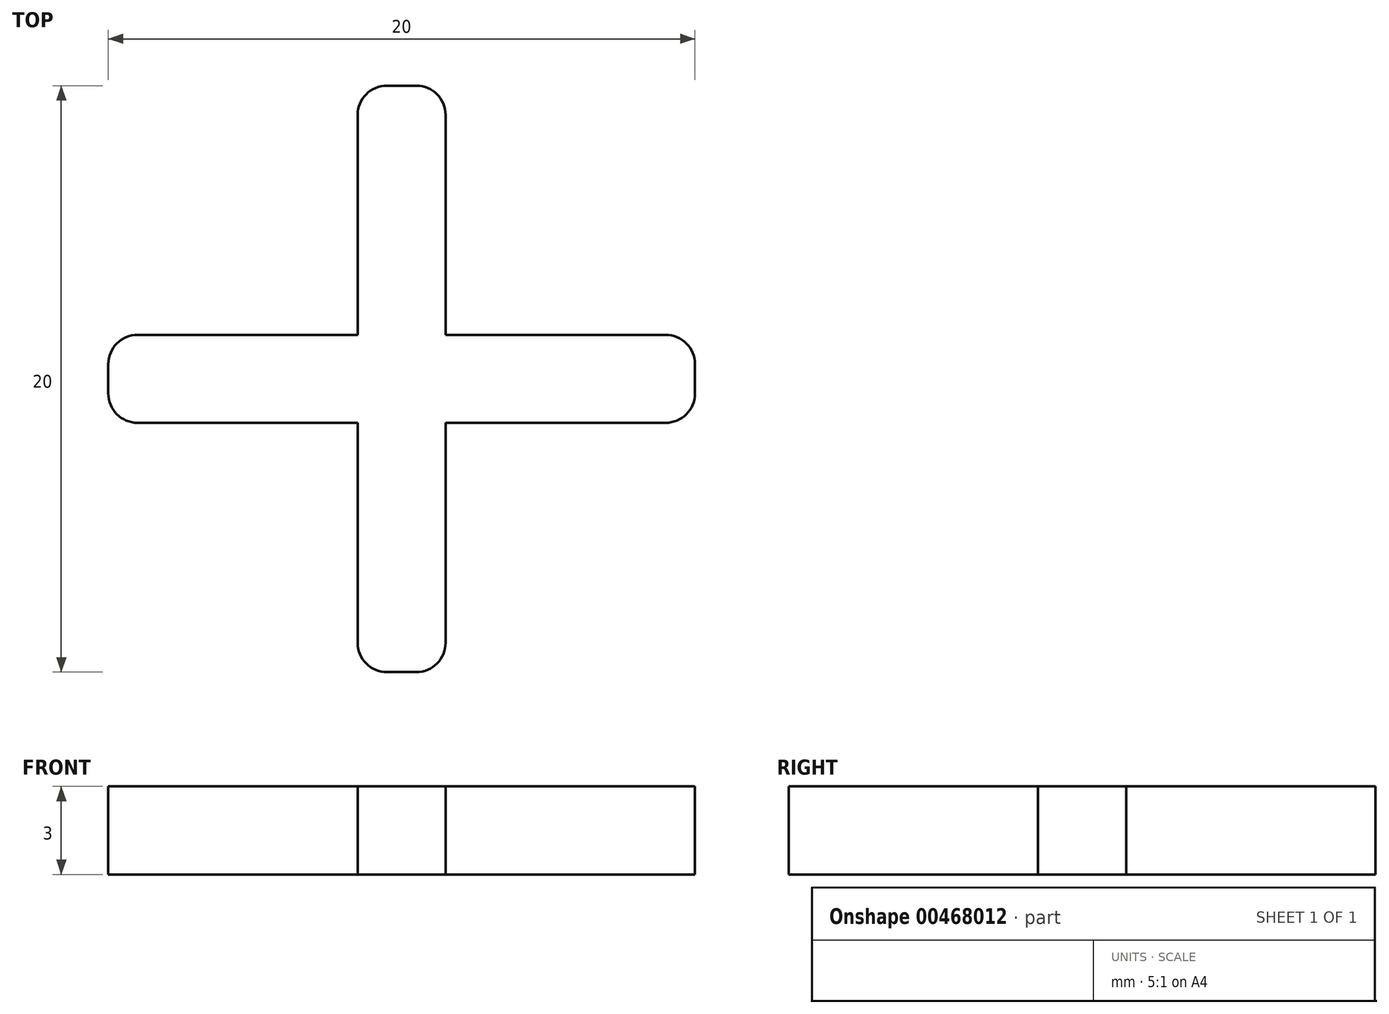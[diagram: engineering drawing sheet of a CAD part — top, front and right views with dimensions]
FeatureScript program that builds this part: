
annotation { "Feature Type Name" : "Feature", "Feature Type Description" : "" }
export const myFeature = defineFeature(function(context is Context, id is Id, definition is map)
    precondition{}
    {
        {
            var Q0;
            Q0=qCreatedBy(makeId("Top.planeOp"),FACE);
            var sketch = newSketch(context, id + "F0", { "sketchPlane" : qUnion([Q0])});
            skLineSegment(sketch, "E0.bottom", {"start": v(10, -1.5) * mm, "end": v(-10, -1.5) * mm});
            skLineSegment(sketch, "E0.top", {"start": v(10, 1.5) * mm, "end": v(-10, 1.5) * mm});
            skLineSegment(sketch, "E0.left", {"start": v(10, -1.5) * mm, "end": v(10, 1.5) * mm});
            skLineSegment(sketch, "E0.right", {"start": v(-10, -1.5) * mm, "end": v(-10, 1.5) * mm});
            skPoint(sketch, "E0.middle", {"position": v(0, 0) * mm});
            skLineSegment(sketch, "E1.bottom", {"start": v(1.5, -10) * mm, "end": v(-1.5, -10) * mm});
            skLineSegment(sketch, "E1.top", {"start": v(1.5, 10) * mm, "end": v(-1.5, 10) * mm});
            skLineSegment(sketch, "E1.left", {"start": v(1.5, -10) * mm, "end": v(1.5, 10) * mm});
            skLineSegment(sketch, "E1.right", {"start": v(-1.5, -10) * mm, "end": v(-1.5, 10) * mm});
            skSolve(sketch);
        }
        {
            var Q0;
            {var subQ5=sQuery(id+"F0.wireOp",EDGE,"E1.top");Q0=makeQuery(id+"F0.imprint","IMPRINT",FACE,{"disambiguationData":[TD([[makeQuery(id+"F0.imprint","IMPRINT",EDGE,{"derivedFrom":subQ5}),1.0]])]});}
            var Q1;
            {var subQ0=sQuery(id+"F0.wireOp",EDGE,"E0.right");Q1=makeQuery(id+"F0.imprint","IMPRINT",FACE,{"disambiguationData":[TD([[makeQuery(id+"F0.imprint","IMPRINT",EDGE,{"derivedFrom":subQ0}),-1.0]])]});}
            var Q2;
            {var subQ0=sQuery(id+"F0.wireOp",EDGE,"E1.left");var subQ1=sQuery(id+"F0.wireOp",EDGE,"E0.bottom");var subQ2=makeQuery(id+"F0.imprint","INTERSECT",VERTEX,{"derivedFrom":[subQ1,subQ0]});Q2=makeQuery(id+"F0.imprint","IMPRINT",FACE,{"disambiguationData":[TD([[makeQuery(id+"F0.imprint","IMPRINT",EDGE,{"disambiguationData":[TD([[subQ2,-1.0]])],"derivedFrom":subQ1}),-1.0]])]});}
            var Q3;
            {var subQ0=sQuery(id+"F0.wireOp",EDGE,"E0.left");Q3=makeQuery(id+"F0.imprint","IMPRINT",FACE,{"disambiguationData":[TD([[makeQuery(id+"F0.imprint","IMPRINT",EDGE,{"derivedFrom":subQ0}),1.0]])]});}
            var Q4;
            {var subQ5=sQuery(id+"F0.wireOp",EDGE,"E1.bottom");Q4=makeQuery(id+"F0.imprint","IMPRINT",FACE,{"disambiguationData":[TD([[makeQuery(id+"F0.imprint","IMPRINT",EDGE,{"derivedFrom":subQ5}),-1.0]])]});}
            extrude(context, id + "F1", {"entities" : qUnion([Q0, Q1, Q2, Q3, Q4]), "depth" : 3 * mm, "offsetDistance" : 25 * mm});
        }
        {
            var Q0;
            Q0=makeQuery(id+"F1.opExtrude","SWEPT_EDGE",EDGE,{"disambiguationData":[OSD([sQuery(id+"F0.wireOp",EDGE,"E0.top"),sQuery(id+"F0.wireOp",EDGE,"E0.right")])]});
            var Q1;
            Q1=makeQuery(id+"F1.opExtrude","SWEPT_EDGE",EDGE,{"disambiguationData":[OSD([sQuery(id+"F0.wireOp",EDGE,"E0.bottom"),sQuery(id+"F0.wireOp",EDGE,"E0.right")])]});
            var Q2;
            Q2=makeQuery(id+"F1.opExtrude","SWEPT_EDGE",EDGE,{"disambiguationData":[OSD([sQuery(id+"F0.wireOp",EDGE,"E1.bottom"),sQuery(id+"F0.wireOp",EDGE,"E1.right")])]});
            var Q3;
            Q3=makeQuery(id+"F1.opExtrude","SWEPT_EDGE",EDGE,{"disambiguationData":[OSD([sQuery(id+"F0.wireOp",EDGE,"E1.top"),sQuery(id+"F0.wireOp",EDGE,"E1.right")])]});
            var Q4;
            Q4=makeQuery(id+"F1.opExtrude","SWEPT_EDGE",EDGE,{"disambiguationData":[OSD([sQuery(id+"F0.wireOp",EDGE,"E1.top"),sQuery(id+"F0.wireOp",EDGE,"E1.left")])]});
            var Q5;
            Q5=makeQuery(id+"F1.opExtrude","SWEPT_EDGE",EDGE,{"disambiguationData":[OSD([sQuery(id+"F0.wireOp",EDGE,"E0.top"),sQuery(id+"F0.wireOp",EDGE,"E0.left")])]});
            var Q6;
            Q6=makeQuery(id+"F1.opExtrude","SWEPT_EDGE",EDGE,{"disambiguationData":[OSD([sQuery(id+"F0.wireOp",EDGE,"E1.bottom"),sQuery(id+"F0.wireOp",EDGE,"E1.left")])]});
            var Q7;
            Q7=makeQuery(id+"F1.opExtrude","SWEPT_EDGE",EDGE,{"disambiguationData":[OSD([sQuery(id+"F0.wireOp",EDGE,"E0.bottom"),sQuery(id+"F0.wireOp",EDGE,"E0.left")])]});
            fillet(context, id + "F2", {"entities" : qUnion([Q0, Q1, Q2, Q3, Q4, Q5, Q6, Q7]), "radius" : 1 * mm, "tangentPropagation" : true, "allowEdgeOverflow" : false});
        }
    });
